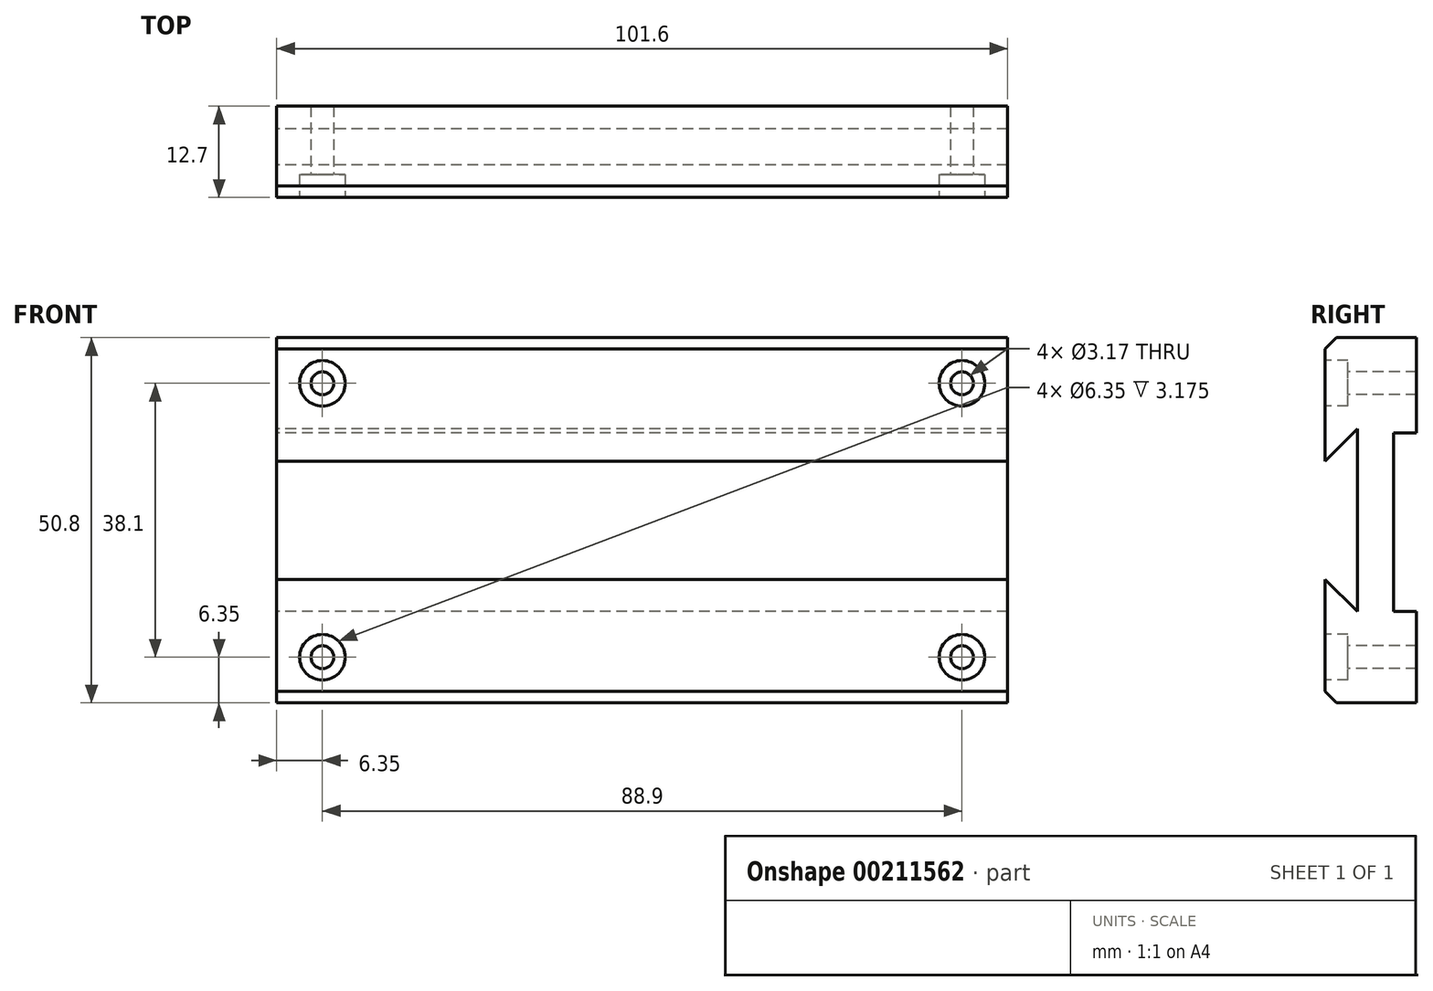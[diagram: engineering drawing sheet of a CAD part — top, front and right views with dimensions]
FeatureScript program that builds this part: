
annotation { "Feature Type Name" : "Feature", "Feature Type Description" : "" }
export const myFeature = defineFeature(function(context is Context, id is Id, definition is map)
    precondition{}
    {
        {
            var Q0;
            Q0=qCreatedBy(makeId("Front.planeOp"),FACE);
            var sketch = newSketch(context, id + "F0", { "sketchPlane" : qUnion([Q0])});
            skLineSegment(sketch, "E0.bottom", {"start": v(0, 0) * mm, "end": v(101.6, 0) * mm});
            skLineSegment(sketch, "E0.top", {"start": v(0, 50.8) * mm, "end": v(101.6, 50.8) * mm});
            skLineSegment(sketch, "E0.left", {"start": v(0, 0) * mm, "end": v(0, 50.8) * mm});
            skLineSegment(sketch, "E0.right", {"start": v(101.6, 0) * mm, "end": v(101.6, 50.8) * mm});
            skSolve(sketch);
        }
        {
            var Q0;
            Q0=makeQuery(id+"F0.imprint","IMPRINT",FACE,{"disambiguationData":[TD([[makeQuery(id+"F0.imprint","IMPRINT",EDGE,{"derivedFrom":sQuery(id+"F0.wireOp",EDGE,"E0.bottom")}),1.0]])]});
            extrude(context, id + "F1", {"entities" : qUnion([Q0]), "depth" : 12.7 * mm});
        }
        {
            var Q0;
            Q0=makeQuery(id+"F1.opExtrude","CAP_EDGE",EDGE,{"disambiguationData":[OSD([sQuery(id+"F0.wireOp",EDGE,"E0.top")])],"isStart":false});
            var Q1;
            Q1=makeQuery(id+"F1.opExtrude","CAP_EDGE",EDGE,{"disambiguationData":[OSD([sQuery(id+"F0.wireOp",EDGE,"E0.bottom")])],"isStart":false});
            chamfer(context, id + "F2", {"entities" : qUnion([Q0, Q1]), "width" : 1.59 * mm, "tangentPropagation" : true});
        }
        {
            var Q0;
            Q0=makeQuery(id+"F1.opExtrude","CAP_FACE",FACE,{"disambiguationData":[OSD([sQuery(id+"F0.wireOp",EDGE,"E0.bottom"),sQuery(id+"F0.wireOp",EDGE,"E0.top"),sQuery(id+"F0.wireOp",EDGE,"E0.left"),sQuery(id+"F0.wireOp",EDGE,"E0.right")])],"isStart":false});
            var sketch = newSketch(context, id + "F3", { "sketchPlane" : qUnion([Q0])});
            skPoint(sketch, "E1", {"position": v(6.35, 6.35) * mm});
            skPoint(sketch, "E2.MirrorP", {"position": v(6.35, 44.45) * mm});
            skPoint(sketch, "E3.MirrorP", {"position": v(95.25, 44.45) * mm});
            skPoint(sketch, "E4.MirrorP", {"position": v(95.25, 6.35) * mm});
            skSolve(sketch);
        }
        {
            var Q0;
            Q0=sQuery(id+"F3.wireOp",VERTEX,"E1");
            var Q1;
            Q1=sQuery(id+"F3.wireOp",VERTEX,"E2.MirrorP");
            var Q2;
            Q2=sQuery(id+"F3.wireOp",VERTEX,"E3.MirrorP");
            var Q3;
            Q3=sQuery(id+"F3.wireOp",VERTEX,"E4.MirrorP");
            var Q4;
            Q4=makeQuery(id+"F1.opExtrude","SWEPT_BODY",BODY,{"disambiguationData":[OSD([sQuery(id+"F0.wireOp",EDGE,"E0.bottom"),sQuery(id+"F0.wireOp",EDGE,"E0.top"),sQuery(id+"F0.wireOp",EDGE,"E0.left"),sQuery(id+"F0.wireOp",EDGE,"E0.right")])]});
            hole(context, id + "F4", {"style" : HoleStyle.C_BORE, "endStyle" : HoleEndStyle.THROUGH, "holeDiameter" : 3.17 * mm, "cBoreDiameter" : 6.35 * mm, "cBoreDepth" : 3.17 * mm, "locations" : qUnion([Q0, Q1, Q2, Q3]), "scope" : qUnion([Q4]), "isTappedThrough" : true});
        }
        {
            var Q0;
            Q0=makeQuery(id+"F1.opExtrude","SWEPT_FACE",FACE,{"disambiguationData":[OSD([sQuery(id+"F0.wireOp",EDGE,"E0.left")])]});
            var sketch = newSketch(context, id + "F5", { "sketchPlane" : qUnion([Q0])});
            skLineSegment(sketch, "E5", {"start": v(12.7, 33.6) * mm, "end": v(8.2, 38.1) * mm});
            skLineSegment(sketch, "E6", {"start": v(8.2, 38.1) * mm, "end": v(8.2, 12.7) * mm});
            skLineSegment(sketch, "E7", {"start": v(8.2, 12.7) * mm, "end": v(12.7, 17.2) * mm});
            skLineSegment(sketch, "E8", {"start": v(12.7, 17.2) * mm, "end": v(12.7, 33.6) * mm});
            skSolve(sketch);
        }
        {
            var Q0;
            Q0=makeQuery(id+"F5.imprint","IMPRINT",FACE,{"disambiguationData":[TD([[makeQuery(id+"F5.imprint","IMPRINT",EDGE,{"derivedFrom":sQuery(id+"F5.wireOp",EDGE,"E5")}),1.0]])]});
            extrude(context, id + "F6", {"entities" : qUnion([Q0]), "operationType" : NewBodyOperationType.REMOVE, "endBound" : BoundingType.THROUGH_ALL, "oppositeDirection" : true, "depth" : 25.4 * mm});
        }
        {
            var Q0;
            Q0=makeQuery(id+"F1.opExtrude","SWEPT_FACE",FACE,{"disambiguationData":[OSD([sQuery(id+"F0.wireOp",EDGE,"E0.left")])]});
            var sketch = newSketch(context, id + "F7", { "sketchPlane" : qUnion([Q0])});
            skLineSegment(sketch, "E9", {"start": v(3.17, 37.54) * mm, "end": v(3.17, 12.7) * mm});
            skLineSegment(sketch, "E10", {"start": v(3.17, 12.7) * mm, "end": v(0, 12.7) * mm});
            skLineSegment(sketch, "E11", {"start": v(3.17, 37.54) * mm, "end": v(0, 37.54) * mm});
            skLineSegment(sketch, "E12", {"start": v(0, 37.54) * mm, "end": v(0, 12.7) * mm});
            skSolve(sketch);
        }
        {
            var Q0;
            Q0 = qSketchRegion(id + "F7", true);
            var Q1;
            Q1=makeQuery(id+"F1.opExtrude","SWEPT_FACE",FACE,{"disambiguationData":[OSD([sQuery(id+"F0.wireOp",EDGE,"E0.right")])]});
            extrude(context, id + "F8", {"entities" : qUnion([Q0]), "operationType" : NewBodyOperationType.REMOVE, "endBound" : BoundingType.UP_TO_SURFACE, "oppositeDirection" : true, "endBoundEntityFace" : qUnion([Q1]), "depth" : 25.4 * mm});
        }
    });
